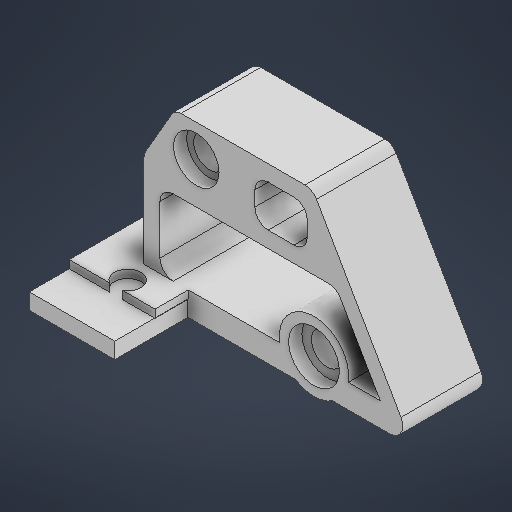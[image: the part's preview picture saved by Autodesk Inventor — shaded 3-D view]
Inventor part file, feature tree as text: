
AUTODESK INVENTOR PART (.ipt)
format: ipt  version: 2025.3 (Build 293356000, 356)  size: 465,920 bytes
history: native  units: in
note: dims shown in document units (in); Inventor stores cm internally (conversion verified against a paired STEP export)
features: extrude x12, sketch x6, fillet x6, projected_geometry x4, other x3
ambient origin geometry x8: Origin, YZ Plane, XZ Plane, XY Plane, X Axis, Y Axis, Z Axis, Center Point
bodies: Solid1 (feature_tree)
feature tree (31):
  other  "EngineMount - Big hole.ipt"
  sketch  "Sketch1"  dims[d0=0.3937in d2=0.2362in]
  extrude  "Extrusion1"  Depth=0.2362in
  extrude  "Extrusion2"  Depth=0.2362in TaperAngle=0.0deg
  fillet  "Fillet2"  Radius=0.3937in
  fillet  "Fillet3"  Radius=0.1969in
  sketch  "Sketch2"  dims[d3=0.2362in d4=0.2362in d5=0.0in d6=0.3937in d7=0.0in d9=0.1969in]
  extrude  "Extrusion3"  Depth=0.1969in
  extrude  "Extrusion4"  Depth=0.3937in TaperAngle=0.0deg
  sketch  "Sketch4"  dims[d10=0.1969in d11=0.5512in]
  extrude  "Extrusion10"  Depth=1.1811in
  extrude  "Extrusion11"  Depth=0.1969in TaperAngle=0.0deg
  extrude  "Extrusion12"  Depth=0.1969in
  extrude  "Extrusion13"  Depth=0.2362in
  extrude  "Extrusion14"  Depth=0.2362in
  extrude  "Extrusion15"  Depth=0.3937in TaperAngle=0.0deg
  sketch  "Sketch8"  dims[d41=0.1969in d42=1.9685in d43=0.0in d44=0.1969in d45=0.2362in d46=0.2362in d47=0.3937in d48=0.0in d49=0.2362in d50=0.3937in d51=0.0in d52=0.1181in d53=1.1811in d54=0.0in d56=1.0827in d57=0.0in d58=1.1811in d59=0.0in d60=0.2362in d61=1.7717in d62=1.1811in d63=0.0in d64=0.1969in d65=0.1969in d66=0.1969in d67=0.1969in]
  extrude  "Extrusion16"  Depth=0.2362in
  extrude  "Extrusion17"  Depth=0.3937in TaperAngle=0.0deg
  fillet  "Fillet5"  Radius=0.1181in
  fillet  "Fillet6"  Radius=1.1811in
  fillet  "Fillet7"  Radius=1.0827in
  fillet  "Fillet8"  Radius=1.1811in
  other  "Solid1::EngineMount - Big hole.ipt"
  other  "TaggingFeature1"
  projected_geometry  "Projected Loop1"
  projected_geometry  "Projected Loop2"
  projected_geometry  "Projected Loop4"
  sketch  "Sketch6"  dims[d12=0.3937in d13=0.0in d14=0.3937in d15=0.0in]
  sketch  "Sketch7"  dims[d38=1.9685in d39=0.0in d40=1.1811in]
  projected_geometry  "Projected Loop6"
